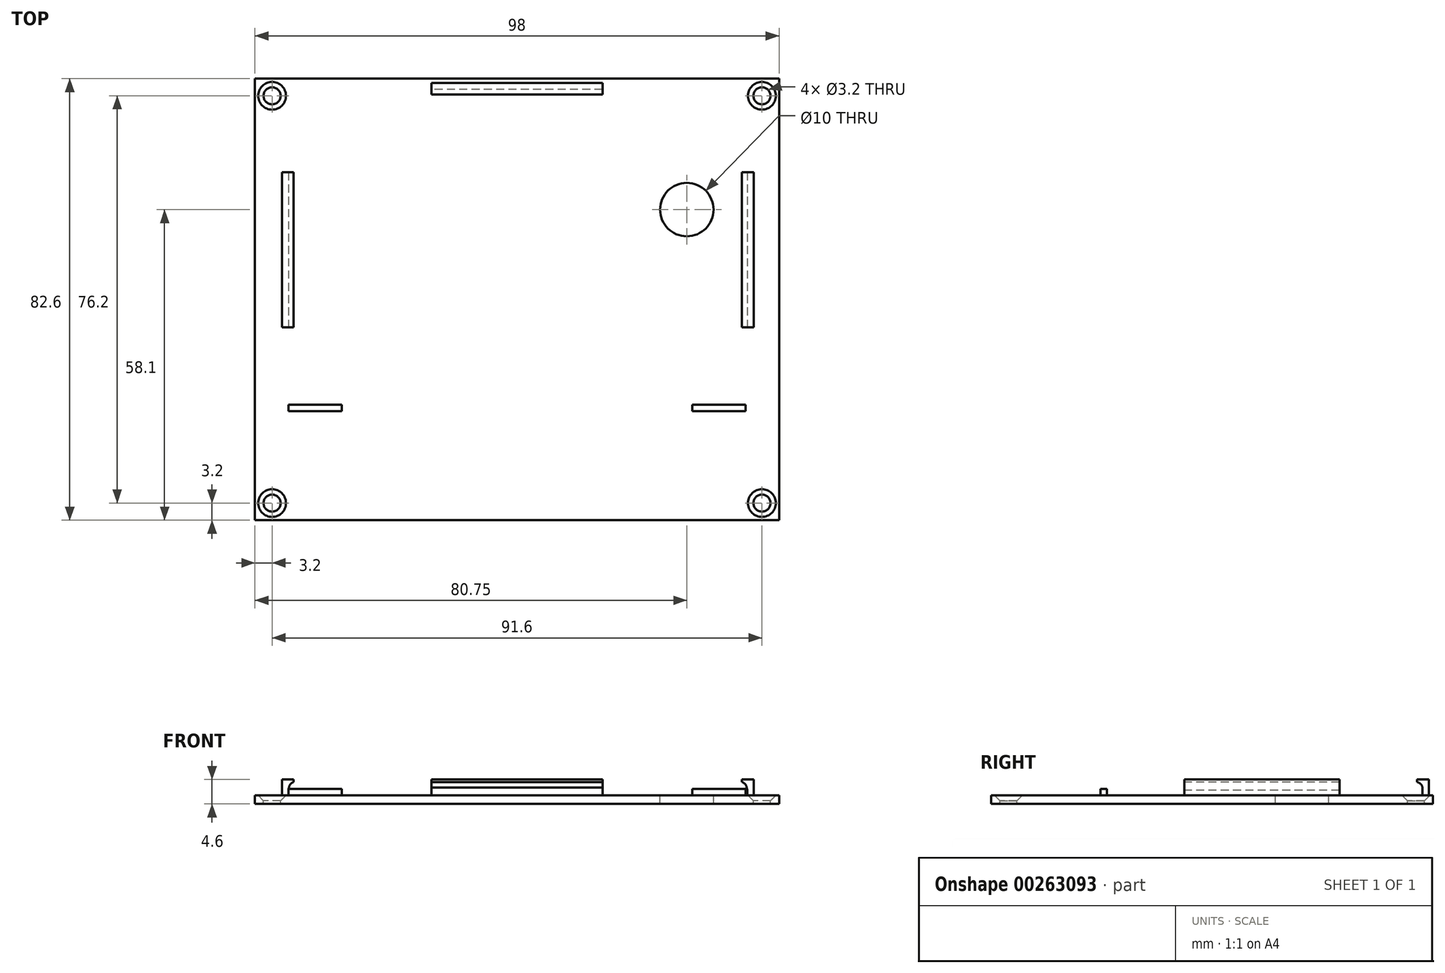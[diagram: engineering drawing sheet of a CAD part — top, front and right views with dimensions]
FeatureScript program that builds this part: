
annotation { "Feature Type Name" : "Feature", "Feature Type Description" : "" }
export const myFeature = defineFeature(function(context is Context, id is Id, definition is map)
    precondition{}
    {
        {
            var Q0;
            Q0=qCreatedBy(makeId("Top.planeOp"),FACE);
            var sketch = newSketch(context, id + "F0", { "sketchPlane" : qUnion([Q0])});
            skLineSegment(sketch, "E0.bottom", {"start": v(0, 0) * mm, "end": v(98, 0) * mm});
            skLineSegment(sketch, "E0.top", {"start": v(0, 82.6) * mm, "end": v(98, 82.6) * mm});
            skLineSegment(sketch, "E0.left", {"start": v(0, 0) * mm, "end": v(0, 82.6) * mm});
            skLineSegment(sketch, "E0.right", {"start": v(98, 0) * mm, "end": v(98, 82.6) * mm});
            skLineSegment(sketch, "E1.bottom", {"start": v(3.2, 79.4) * mm, "end": v(94.8, 79.4) * mm, "construction": true});
            skLineSegment(sketch, "E1.top", {"start": v(3.2, 3.2) * mm, "end": v(94.8, 3.2) * mm, "construction": true});
            skLineSegment(sketch, "E1.left", {"start": v(3.2, 79.4) * mm, "end": v(3.2, 3.2) * mm, "construction": true});
            skLineSegment(sketch, "E1.right", {"start": v(94.8, 79.4) * mm, "end": v(94.8, 3.2) * mm, "construction": true});
            skCircle(sketch, "E2", {"center": v(3.2, 79.4) * mm, "radius": 1.6 * mm});
            skCircle(sketch, "E3", {"center": v(94.8, 79.4) * mm, "radius": 1.6 * mm});
            skCircle(sketch, "E4", {"center": v(94.8, 3.2) * mm, "radius": 1.6 * mm});
            skCircle(sketch, "E5", {"center": v(3.2, 3.2) * mm, "radius": 1.6 * mm});
            skSolve(sketch);
        }
        {
            var Q0;
            Q0=makeQuery(id+"F0.imprint","IMPRINT",FACE,{"disambiguationData":[TD([[makeQuery(id+"F0.imprint","IMPRINT",EDGE,{"derivedFrom":sQuery(id+"F0.wireOp",EDGE,"E0.bottom")}),1.0]])]});
            var sketch = newSketch(context, id + "F1", { "sketchPlane" : qUnion([Q0])});
            skLineSegment(sketch, "E6.bottom", {"start": v(6.25, 80.6) * mm, "end": v(91.75, 80.6) * mm, "construction": true});
            skLineSegment(sketch, "E6.top", {"start": v(6.25, 21.6) * mm, "end": v(91.75, 21.6) * mm, "construction": true});
            skLineSegment(sketch, "E6.left", {"start": v(6.25, 80.6) * mm, "end": v(6.25, 21.6) * mm, "construction": true});
            skLineSegment(sketch, "E6.right", {"start": v(91.75, 80.6) * mm, "end": v(91.75, 21.6) * mm, "construction": true});
            skCircle(sketch, "E7", {"center": v(80.75, 58.1) * mm, "radius": 5 * mm});
            skLineSegment(sketch, "E8", {"start": v(49, 80.6) * mm, "end": v(49, 21.6) * mm, "construction": true});
            skLineSegment(sketch, "E9.bottom", {"start": v(6.25, 21.6) * mm, "end": v(16.25, 21.6) * mm});
            skLineSegment(sketch, "E9.top", {"start": v(6.25, 20.4) * mm, "end": v(16.25, 20.4) * mm});
            skLineSegment(sketch, "E9.left", {"start": v(6.25, 21.6) * mm, "end": v(6.25, 20.4) * mm});
            skLineSegment(sketch, "E9.right", {"start": v(16.25, 21.6) * mm, "end": v(16.25, 20.4) * mm});
            skLineSegment(sketch, "E10.bottom", {"start": v(91.75, 21.6) * mm, "end": v(81.75, 21.6) * mm});
            skLineSegment(sketch, "E10.top", {"start": v(91.75, 20.4) * mm, "end": v(81.75, 20.4) * mm});
            skLineSegment(sketch, "E10.left", {"start": v(91.75, 21.6) * mm, "end": v(91.75, 20.4) * mm});
            skLineSegment(sketch, "E10.right", {"start": v(81.75, 21.6) * mm, "end": v(81.75, 20.4) * mm});
            skSolve(sketch);
        }
        {
            var Q0;
            Q0=makeQuery(id+"F0.imprint","IMPRINT",FACE,{"disambiguationData":[TD([[makeQuery(id+"F0.imprint","IMPRINT",EDGE,{"derivedFrom":sQuery(id+"F0.wireOp",EDGE,"E0.bottom")}),1.0]])]});
            extrude(context, id + "F2", {"entities" : qUnion([Q0]), "oppositeDirection" : true, "depth" : 1.6 * mm});
        }
        {
            var Q0;
            Q0=makeQuery(id+"F1.imprint","IMPRINT",FACE,{"disambiguationData":[TD([[makeQuery(id+"F1.imprint","IMPRINT",EDGE,{"derivedFrom":sQuery(id+"F1.wireOp",EDGE,"E7")}),1.0]])]});
            extrude(context, id + "F3", {"entities" : qUnion([Q0]), "operationType" : NewBodyOperationType.REMOVE, "endBound" : BoundingType.THROUGH_ALL, "oppositeDirection" : true, "depth" : 25 * mm});
        }
        {
            var Q0;
            Q0=qCreatedBy(makeId("Front.planeOp"),FACE);
            var sketch = newSketch(context, id + "F4", { "sketchPlane" : qUnion([Q0])});
            skLineSegment(sketch, "E11", {"start": v(6.25, 0) * mm, "end": v(5.05, 0) * mm});
            skLineSegment(sketch, "E12.bottom", {"start": v(5.05, 0) * mm, "end": v(6.25, 0) * mm});
            skLineSegment(sketch, "E12.top", {"start": v(5.05, 0) * mm, "end": v(6.25, 0) * mm});
            skLineSegment(sketch, "E12.left", {"start": v(5.05, 0) * mm, "end": v(5.05, 0) * mm});
            skLineSegment(sketch, "E12.right", {"start": v(6.25, 0) * mm, "end": v(6.25, 0) * mm});
            skLineSegment(sketch, "E13.bottom", {"start": v(6.25, 3) * mm, "end": v(5.05, 3) * mm});
            skLineSegment(sketch, "E13.left", {"start": v(6.25, 3) * mm, "end": v(6.25, 0) * mm});
            skLineSegment(sketch, "E13.right", {"start": v(5.05, 3) * mm, "end": v(5.05, 0) * mm});
            skLineSegment(sketch, "E14", {"start": v(6.25, 3) * mm, "end": v(7.25, 3) * mm});
            skLineSegment(sketch, "E15", {"start": v(7.25, 3) * mm, "end": v(7.25, 2.5) * mm});
            skFitSpline(sketch, "E16", {"points": [v(7.25, 2.5) * mm, v(6.25, 0) * mm], "startDerivative": vector(-3.78, -0.96) * mm, "endDerivative": vector(0, -0.48) * mm});
            skLineSegment(sketch, "E17", {"start": v(49.15, 0) * mm, "end": v(49.15, 10.87) * mm, "construction": true});
            skLineSegment(sketch, "E18.MirrorCS", {"start": v(92.05, 3) * mm, "end": v(93.25, 3) * mm});
            skLineSegment(sketch, "E19.MirrorCS", {"start": v(92.05, 3) * mm, "end": v(91.05, 3) * mm});
            skLineSegment(sketch, "E20.MirrorCS", {"start": v(91.05, 3) * mm, "end": v(91.05, 2.5) * mm});
            skLineSegment(sketch, "E21.MirrorCS", {"start": v(92.05, 3) * mm, "end": v(92.05, 0) * mm});
            skFitSpline(sketch, "E22.MirrorCS", {"points": [v(91.05, 2.5) * mm, v(92.05, 0) * mm], "startDerivative": vector(3.78, -0.96) * mm, "endDerivative": vector(0, -0.48) * mm});
            skLineSegment(sketch, "E23.MirrorCS", {"start": v(92.05, 0) * mm, "end": v(93.25, 0) * mm});
            skLineSegment(sketch, "E24.MirrorCS", {"start": v(93.25, 3) * mm, "end": v(93.25, 0) * mm});
            skSolve(sketch);
        }
        {
            var Q0;
            Q0=qSketchRegion(id+"F4",true);
            extrude(context, id + "F5", {"entities" : qUnion([Q0]), "operationType" : NewBodyOperationType.ADD, "oppositeDirection" : true, "depth" : 65.1 * mm, "hasSecondDirection" : true, "secondDirectionOppositeDirection" : true, "secondDirectionDepth" : 36.1 * mm});
        }
        {
            var Q0;
            Q0=qCreatedBy(makeId("Right.planeOp"),FACE);
            var sketch = newSketch(context, id + "F6", { "sketchPlane" : qUnion([Q0])});
            skLineSegment(sketch, "E25.bottom", {"start": v(80.62, 0) * mm, "end": v(81.82, 0) * mm});
            skLineSegment(sketch, "E25.top", {"start": v(80.62, 3) * mm, "end": v(81.82, 3) * mm});
            skLineSegment(sketch, "E25.left", {"start": v(80.62, 0) * mm, "end": v(80.62, 3) * mm});
            skLineSegment(sketch, "E25.right", {"start": v(81.82, 0) * mm, "end": v(81.82, 3) * mm});
            skLineSegment(sketch, "E26", {"start": v(80.62, 3) * mm, "end": v(79.62, 3) * mm});
            skLineSegment(sketch, "E27", {"start": v(79.62, 3) * mm, "end": v(79.62, 2.5) * mm});
            skFitSpline(sketch, "E28", {"points": [v(79.62, 2.5) * mm, v(80.62, 1.5) * mm, v(80.62, 0) * mm], "startDerivative": vector(3.74, -1.12) * mm, "endDerivative": vector(0, -1.77) * mm});
            skSolve(sketch);
        }
        {
            var Q0;
            Q0=qSketchRegion(id+"F6",true);
            extrude(context, id + "F7", {"entities" : qUnion([Q0]), "operationType" : NewBodyOperationType.ADD, "depth" : 65 * mm, "hasSecondDirection" : true, "secondDirectionOppositeDirection" : false, "secondDirectionDepth" : 33 * mm});
        }
        {
            var Q0;
            Q0=makeQuery(id+"F1.imprint","IMPRINT",FACE,{"disambiguationData":[TD([[makeQuery(id+"F1.imprint","IMPRINT",EDGE,{"derivedFrom":sQuery(id+"F1.wireOp",EDGE,"E9.bottom")}),-1.0]])]});
            var Q1;
            Q1=makeQuery(id+"F1.imprint","IMPRINT",FACE,{"disambiguationData":[TD([[makeQuery(id+"F1.imprint","IMPRINT",EDGE,{"derivedFrom":sQuery(id+"F1.wireOp",EDGE,"E10.bottom")}),1.0]])]});
            extrude(context, id + "F8", {"entities" : qUnion([Q0, Q1]), "operationType" : NewBodyOperationType.ADD, "depth" : 1.2 * mm});
        }
        {
            var Q0;
            Q0=makeQuery(id+"F2.opExtrude","CAP_EDGE",EDGE,{"disambiguationData":[OSD([sQuery(id+"F0.wireOp",EDGE,"E2")])],"isStart":true});
            var Q1;
            Q1=makeQuery(id+"F2.opExtrude","CAP_EDGE",EDGE,{"disambiguationData":[OSD([sQuery(id+"F0.wireOp",EDGE,"E5")])],"isStart":true});
            var Q2;
            Q2=makeQuery(id+"F2.opExtrude","CAP_EDGE",EDGE,{"disambiguationData":[OSD([sQuery(id+"F0.wireOp",EDGE,"E4")])],"isStart":true});
            var Q3;
            Q3=makeQuery(id+"F2.opExtrude","CAP_EDGE",EDGE,{"disambiguationData":[OSD([sQuery(id+"F0.wireOp",EDGE,"E3")])],"isStart":true});
            chamfer(context, id + "F9", {"entities" : qUnion([Q0, Q1, Q2, Q3]), "width" : 1 * mm, "tangentPropagation" : true});
        }
    });
